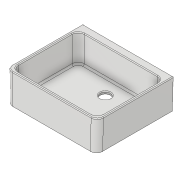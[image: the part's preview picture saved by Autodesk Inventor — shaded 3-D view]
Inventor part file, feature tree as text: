
AUTODESK INVENTOR PART (.ipt)
format: ipt  version: 2018 (Build 220112000, 112)  size: 216,064 bytes
history: native  units: in
note: dims shown in document units (in); Inventor stores cm internally (conversion verified against a paired STEP export)
features: fillet x4, sketch x4, extrude x3, hole x1, projected_geometry x1
ambient origin geometry x8: Origin, YZ Plane, XZ Plane, XY Plane, X Axis, Y Axis, Z Axis, Center Point
bodies: Solid1 (feature_tree)
feature tree (13):
  extrude  "Extrusion1"  Depth=19.685in
  extrude  "Extrusion2"  Depth=21.8504in
  extrude  "Extrusion3"  Depth=7.0866in TaperAngle=0.0deg
  fillet  "Fillet1"  Radius=23.0315in
  fillet  "Fillet2"  Radius=7.0866in
  fillet  "Fillet3"  Radius=1.5748in
  hole  "Hole1"  [1 undecoded]
  fillet  "Fillet4"  Radius=0.7874in
  sketch  "Sketch1"  dims[d0=23.4252in d1=19.685in]
  sketch  "Sketch2"  dims[d2=7.874in d3=0.0in d4=21.8504in]
  sketch  "Sketch3"  dims[d5=16.9291in d6=7.0866in d7=0.0in d8=23.0315in d9=7.0866in d10=0.0in d11=1.5748in]
  projected_geometry  "Projected Loop1"
  sketch  "Sketch4"  dims[d12=0.7874in d13=23.4252in d14=0.7874in d15=0.1969in d16=0.3937in d18=5.9055in d19=2.5591in d20=0.2362in d21=0.1575in d22=0.0787in d23=90.0deg d24=0.315in d25=0.8108in d27=21.063in d28=10.5315in d29=0.1969in]
note: 1 required parameter value undecoded (feature->parameter linkage not recoverable at this tier; creation-order binding heuristic only, values carry confidence <= 0.55)
